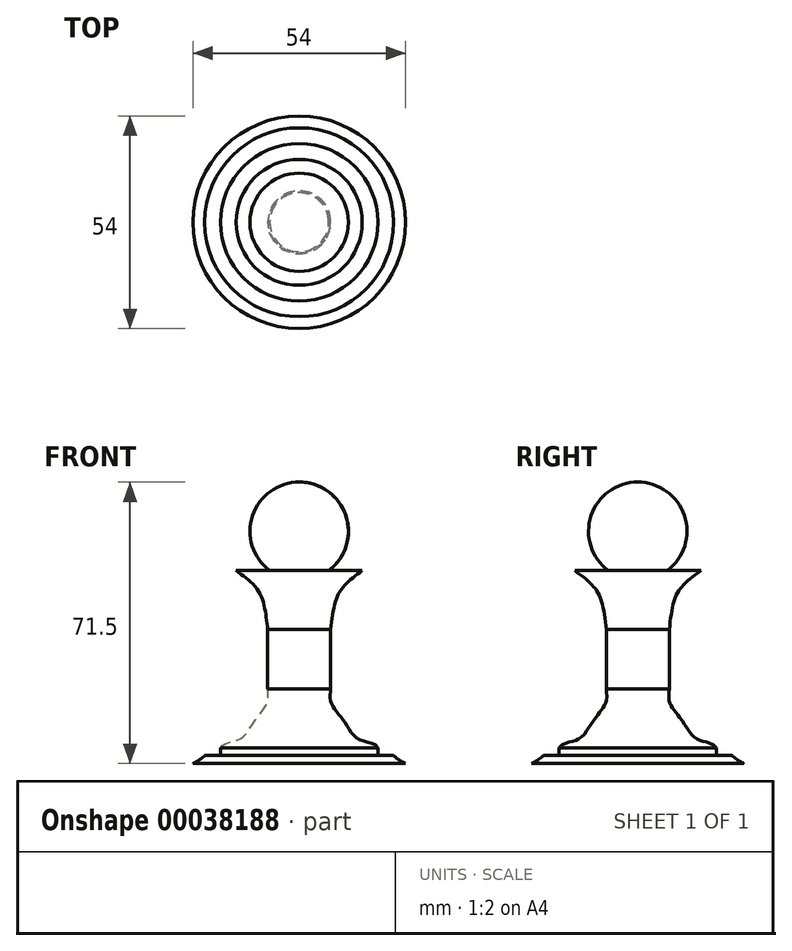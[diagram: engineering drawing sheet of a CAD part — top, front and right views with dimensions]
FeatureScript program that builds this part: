
annotation { "Feature Type Name" : "Feature", "Feature Type Description" : "" }
export const myFeature = defineFeature(function(context is Context, id is Id, definition is map)
    precondition{}
    {
        {
            var Q0;
            Q0=qCreatedBy(makeId("Front.planeOp"),FACE);
            var sketch = newSketch(context, id + "F0", { "sketchPlane" : qUnion([Q0])});
            skArc(sketch, "E0", {"start": v(-42.86, 23) * mm, "mid": v(-38.5, 36.95) * mm, "end": v(-50.36, 45.5) * mm});
            skLineSegment(sketch, "E1", {"start": v(-50.36, 33) * mm, "end": v(-50.36, 23) * mm});
            skLineSegment(sketch, "E2", {"start": v(-42.86, 23) * mm, "end": v(-34.36, 23) * mm});
            skLineSegment(sketch, "E3", {"start": v(-50.36, 23) * mm, "end": v(-50.36, 8) * mm});
            skLineSegment(sketch, "E4", {"start": v(-42.36, 8) * mm, "end": v(-42.36, -7) * mm});
            skLineSegment(sketch, "E5", {"start": v(-50.36, -7) * mm, "end": v(-50.36, -22) * mm});
            skLineSegment(sketch, "E6", {"start": v(-30.36, -24) * mm, "end": v(-26.36, -24) * mm});
            skLineSegment(sketch, "E7", {"start": v(-50.36, -22) * mm, "end": v(-50.36, -24) * mm});
            skLineSegment(sketch, "E8", {"start": v(-30.36, -22) * mm, "end": v(-30.36, -24) * mm});
            skLineSegment(sketch, "E9", {"start": v(-50.36, -26) * mm, "end": v(-23.36, -26) * mm});
            skLineSegment(sketch, "E10", {"start": v(-50.36, -24) * mm, "end": v(-50.36, -26) * mm});
            skFitSpline(sketch, "E11", {"points": [v(-34.36, 23) * mm, v(-38.54, 19.6) * mm, v(-40.97, 15.78) * mm, v(-42.36, 8) * mm], "startDerivative": vector(-14.1, -10.4) * mm, "endDerivative": vector(-2.53, -22.03) * mm});
            skFitSpline(sketch, "E12", {"points": [v(-42.36, -7) * mm, v(-42.36, -10.1) * mm, v(-40.8, -12.88) * mm, v(-38.37, -16.18) * mm, v(-35.24, -19.83) * mm, v(-30.36, -22) * mm], "startDerivative": vector(-1.96, -17.99) * mm, "endDerivative": vector(11.07, -18.42) * mm});
            skFitSpline(sketch, "E13", {"points": [v(-26.36, -24) * mm, v(-25.18, -25) * mm, v(-23.36, -26) * mm], "startDerivative": vector(2.37, -2.21) * mm, "endDerivative": vector(3.6, -1.8) * mm});
            skLineSegment(sketch, "E14", {"start": v(-50.36, 20.5) * mm, "end": v(-50.36, 45.5) * mm});
            skLineSegment(sketch, "E15", {"start": v(-50.36, 8) * mm, "end": v(-50.36, -7) * mm});
            skSolve(sketch);
        }
        {
            var Q0;
            {var subQ2=sQuery(id+"F0.wireOp",EDGE,"E0");Q0=makeQuery(id+"F0.imprint","IMPRINT",FACE,{"disambiguationData":[TD([[makeQuery(id+"F0.imprint","IMPRINT",EDGE,{"derivedFrom":subQ2}),1.0]])]});}
            var Q1;
            Q1=sQuery(id+"F0.wireOp",EDGE,"E7");
            revolve(context, id + "F1", {"entities" : qUnion([Q0]), "axis" : qUnion([Q1]), "revolveType" : RevolveType.FULL});
        }
    });
